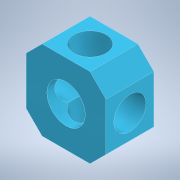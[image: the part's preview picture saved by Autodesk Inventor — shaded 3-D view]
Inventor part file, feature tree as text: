
AUTODESK INVENTOR PART (.ipt)
format: ipt  version: 2022 (Build 260153000, 153)  size: 156,160 bytes
history: native  units: in
note: dims shown in document units (in); Inventor stores cm internally (conversion verified against a paired STEP export)
features: sketch x5, extrude x4, chamfer x1
ambient origin geometry x8: Origin, YZ Plane, XZ Plane, XY Plane, X Axis, Y Axis, Z Axis, Center Point
bodies: Solid1 (feature_tree)
feature tree (10):
  sketch  "Sketch1"  dims[d0=0.9843in d1=0.9843in d2=0.5906in d3=0.0in]
  extrude  "Extrusion1"  Depth=0.9843in
  chamfer  "Chamfer1"  Distance=0.5906in
  extrude  "Extrusion2"  Depth=0.4724in
  extrude  "Extrusion3"  Depth=0.4921in
  extrude  "Extrusion4"  Depth=0.3976in
  sketch  "Sketch2"  dims[d4=0.1969in d5=0.0787in d6=45.0deg d7=0.4724in]
  sketch  "Sketch3"  dims[d8=0.4921in d9=0.4921in]
  sketch  "Sketch4"  dims[d10=0.5906in d11=0.0in d12=0.3976in]
  sketch  "Sketch5"  dims[d13=0.4921in d14=0.2953in d15=0.0in d16=0.0in d17=0.3976in d18=0.2953in d19=0.4921in d20=0.0in d21=0.0in]
